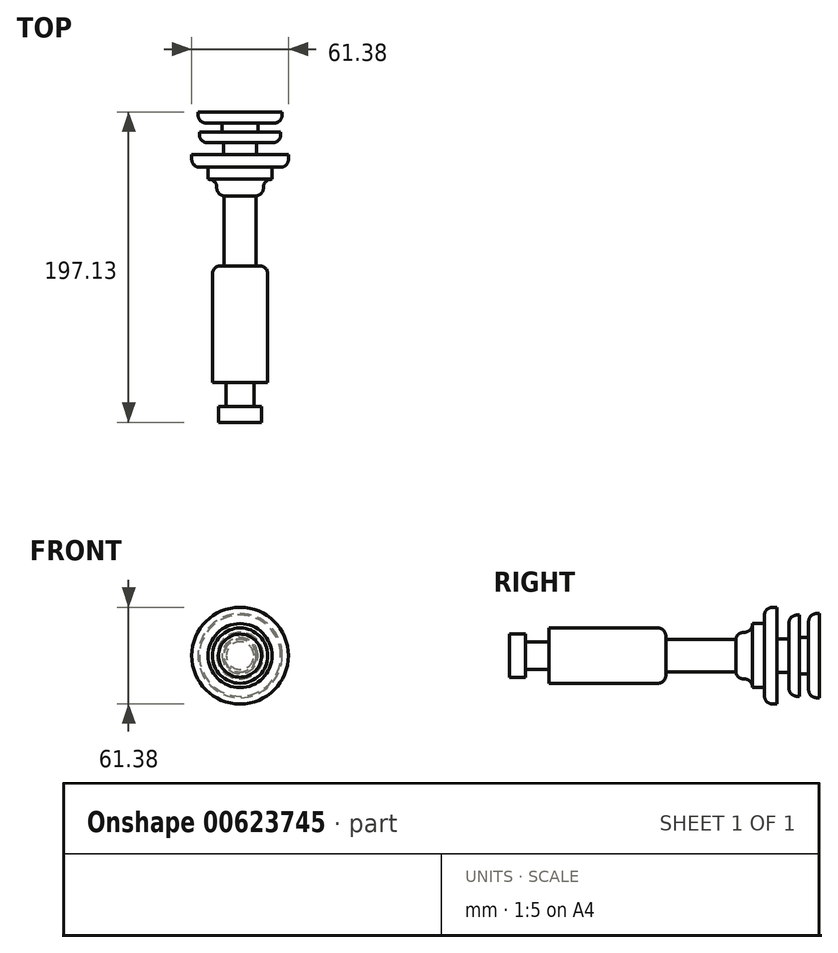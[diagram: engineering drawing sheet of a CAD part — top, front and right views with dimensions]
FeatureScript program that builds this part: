
annotation { "Feature Type Name" : "Feature", "Feature Type Description" : "" }
export const myFeature = defineFeature(function(context is Context, id is Id, definition is map)
    precondition{}
    {
        {
            var Q0;
            Q0=qCreatedBy(makeId("Top.planeOp"),FACE);
            var sketch = newSketch(context, id + "F0", { "sketchPlane" : qUnion([Q0])});
            skLineSegment(sketch, "E0.bottom", {"start": v(0, 53.29) * mm, "end": v(-26.72, 53.29) * mm});
            skLineSegment(sketch, "E0.top", {"start": v(0, 46.27) * mm, "end": v(-26.72, 46.27) * mm});
            skLineSegment(sketch, "E0.left", {"start": v(0, 53.29) * mm, "end": v(0, 46.27) * mm});
            skLineSegment(sketch, "E0.right", {"start": v(-26.72, 53.29) * mm, "end": v(-26.72, 46.27) * mm});
            skLineSegment(sketch, "E1.bottom", {"start": v(0, 46.27) * mm, "end": v(-11.45, 46.27) * mm});
            skLineSegment(sketch, "E1.top", {"start": v(0, 40.46) * mm, "end": v(-11.45, 40.46) * mm});
            skLineSegment(sketch, "E1.left", {"start": v(0, 46.27) * mm, "end": v(0, 40.46) * mm});
            skLineSegment(sketch, "E1.right", {"start": v(-11.45, 46.27) * mm, "end": v(-11.45, 40.46) * mm});
            skLineSegment(sketch, "E2.bottom", {"start": v(0, 40.46) * mm, "end": v(-25.8, 40.46) * mm});
            skLineSegment(sketch, "E2.top", {"start": v(0, 33.74) * mm, "end": v(-25.8, 33.74) * mm});
            skLineSegment(sketch, "E2.left", {"start": v(0, 40.46) * mm, "end": v(0, 33.74) * mm});
            skLineSegment(sketch, "E2.right", {"start": v(-25.8, 40.46) * mm, "end": v(-25.8, 33.74) * mm});
            skLineSegment(sketch, "E3.bottom", {"start": v(0, 33.74) * mm, "end": v(-10.54, 33.74) * mm});
            skLineSegment(sketch, "E3.top", {"start": v(0, 26.11) * mm, "end": v(-10.54, 26.11) * mm});
            skLineSegment(sketch, "E3.left", {"start": v(0, 33.74) * mm, "end": v(0, 26.11) * mm});
            skLineSegment(sketch, "E3.right", {"start": v(-10.54, 33.74) * mm, "end": v(-10.54, 26.11) * mm});
            skLineSegment(sketch, "E4.bottom", {"start": v(0, 26.11) * mm, "end": v(-30.7, 26.11) * mm});
            skLineSegment(sketch, "E4.top", {"start": v(0, 18.17) * mm, "end": v(-30.7, 18.17) * mm});
            skLineSegment(sketch, "E4.left", {"start": v(0, 26.11) * mm, "end": v(0, 18.17) * mm});
            skLineSegment(sketch, "E4.right", {"start": v(-30.7, 26.11) * mm, "end": v(-30.7, 18.17) * mm});
            skLineSegment(sketch, "E5.bottom", {"start": v(0, 18.17) * mm, "end": v(-20.3, 18.17) * mm});
            skLineSegment(sketch, "E5.top", {"start": v(0, 10.54) * mm, "end": v(-20.3, 10.54) * mm});
            skLineSegment(sketch, "E5.left", {"start": v(0, 18.17) * mm, "end": v(0, 10.54) * mm});
            skLineSegment(sketch, "E5.right", {"start": v(-20.3, 18.17) * mm, "end": v(-20.3, 10.54) * mm});
            skLineSegment(sketch, "E6.bottom", {"start": v(0, 10.54) * mm, "end": v(-14.81, 10.54) * mm});
            skLineSegment(sketch, "E6.top", {"start": v(0, 0) * mm, "end": v(-14.81, 0) * mm});
            skLineSegment(sketch, "E6.left", {"start": v(0, 10.54) * mm, "end": v(0, 0) * mm});
            skLineSegment(sketch, "E6.right", {"start": v(-14.81, 10.54) * mm, "end": v(-14.81, 0) * mm});
            skLineSegment(sketch, "E7.bottom", {"start": v(0, 0) * mm, "end": v(-10.23, 0) * mm});
            skLineSegment(sketch, "E7.top", {"start": v(0, -7.48) * mm, "end": v(-10.23, -7.48) * mm});
            skLineSegment(sketch, "E7.left", {"start": v(0, 0) * mm, "end": v(0, -7.48) * mm});
            skLineSegment(sketch, "E7.right", {"start": v(-10.23, 0) * mm, "end": v(-10.23, -7.48) * mm});
            skLineSegment(sketch, "E8.top", {"start": v(0, -44.43) * mm, "end": v(-10.23, -44.43) * mm});
            skLineSegment(sketch, "E8.left", {"start": v(0, -7.48) * mm, "end": v(0, -44.43) * mm});
            skLineSegment(sketch, "E8.right", {"start": v(-10.23, -7.48) * mm, "end": v(-10.23, -44.43) * mm});
            skLineSegment(sketch, "E9.bottom", {"start": v(0, -44.43) * mm, "end": v(-17.56, -44.43) * mm});
            skLineSegment(sketch, "E9.top", {"start": v(0, -118.69) * mm, "end": v(-17.56, -118.69) * mm});
            skLineSegment(sketch, "E9.left", {"start": v(0, -44.43) * mm, "end": v(0, -118.69) * mm});
            skLineSegment(sketch, "E9.right", {"start": v(-17.56, -44.43) * mm, "end": v(-17.56, -118.69) * mm});
            skPoint(sketch, "E10.oppositeSnap0", {"position": v(-8.78, -118.69) * mm});
            skLineSegment(sketch, "E10.bottom", {"start": v(0, -118.69) * mm, "end": v(-8.78, -118.69) * mm});
            skLineSegment(sketch, "E10.top", {"start": v(0, -133.64) * mm, "end": v(-8.78, -133.64) * mm});
            skLineSegment(sketch, "E10.left", {"start": v(0, -118.69) * mm, "end": v(0, -133.64) * mm});
            skLineSegment(sketch, "E10.right", {"start": v(-8.78, -118.69) * mm, "end": v(-8.78, -133.64) * mm});
            skLineSegment(sketch, "E11.bottom", {"start": v(0, -133.64) * mm, "end": v(-13.69, -133.64) * mm});
            skLineSegment(sketch, "E11.top", {"start": v(0, -143.84) * mm, "end": v(-13.69, -143.84) * mm});
            skLineSegment(sketch, "E11.left", {"start": v(0, -133.64) * mm, "end": v(0, -143.84) * mm});
            skLineSegment(sketch, "E11.right", {"start": v(-13.69, -133.64) * mm, "end": v(-13.69, -143.84) * mm});
            skSolve(sketch);
        }
        {
            var Q0;
            Q0 = qSketchRegion(id + "F0", true);
            var Q1;
            Q1=sQuery(id+"F0.wireOp",EDGE,"E7.left");
            revolve(context, id + "F1", {"entities" : qUnion([Q0]), "axis" : qUnion([Q1]), "revolveType" : RevolveType.FULL});
        }
        {
            var Q0;
            Q0=makeQuery(id+"F1.opRevolve","SWEPT_EDGE",EDGE,{"disambiguationData":[OSD([sQuery(id+"F0.wireOp",EDGE,"E9.bottom"),sQuery(id+"F0.wireOp",EDGE,"E9.right")])]});
            var Q1;
            Q1=makeQuery(id+"F1.opRevolve","SWEPT_FACE",FACE,{"disambiguationData":[OSD([sQuery(id+"F0.wireOp",EDGE,"E6.right")])]});
            var Q2;
            Q2=makeQuery(id+"F1.opRevolve","SWEPT_EDGE",EDGE,{"disambiguationData":[OSD([sQuery(id+"F0.wireOp",EDGE,"E4.top"),sQuery(id+"F0.wireOp",EDGE,"E4.right")])]});
            var Q3;
            Q3=makeQuery(id+"F1.opRevolve","SWEPT_EDGE",EDGE,{"disambiguationData":[OSD([sQuery(id+"F0.wireOp",EDGE,"E2.top"),sQuery(id+"F0.wireOp",EDGE,"E2.right")])]});
            var Q4;
            Q4=makeQuery(id+"F1.opRevolve","SWEPT_EDGE",EDGE,{"disambiguationData":[OSD([sQuery(id+"F0.wireOp",EDGE,"E0.top"),sQuery(id+"F0.wireOp",EDGE,"E0.right")])]});
            fillet(context, id + "F2", {"entities" : qUnion([Q0, Q1, Q2, Q3, Q4]), "radius" : 5.08 * mm, "tangentPropagation" : true, "allowEdgeOverflow" : false});
        }
    });
